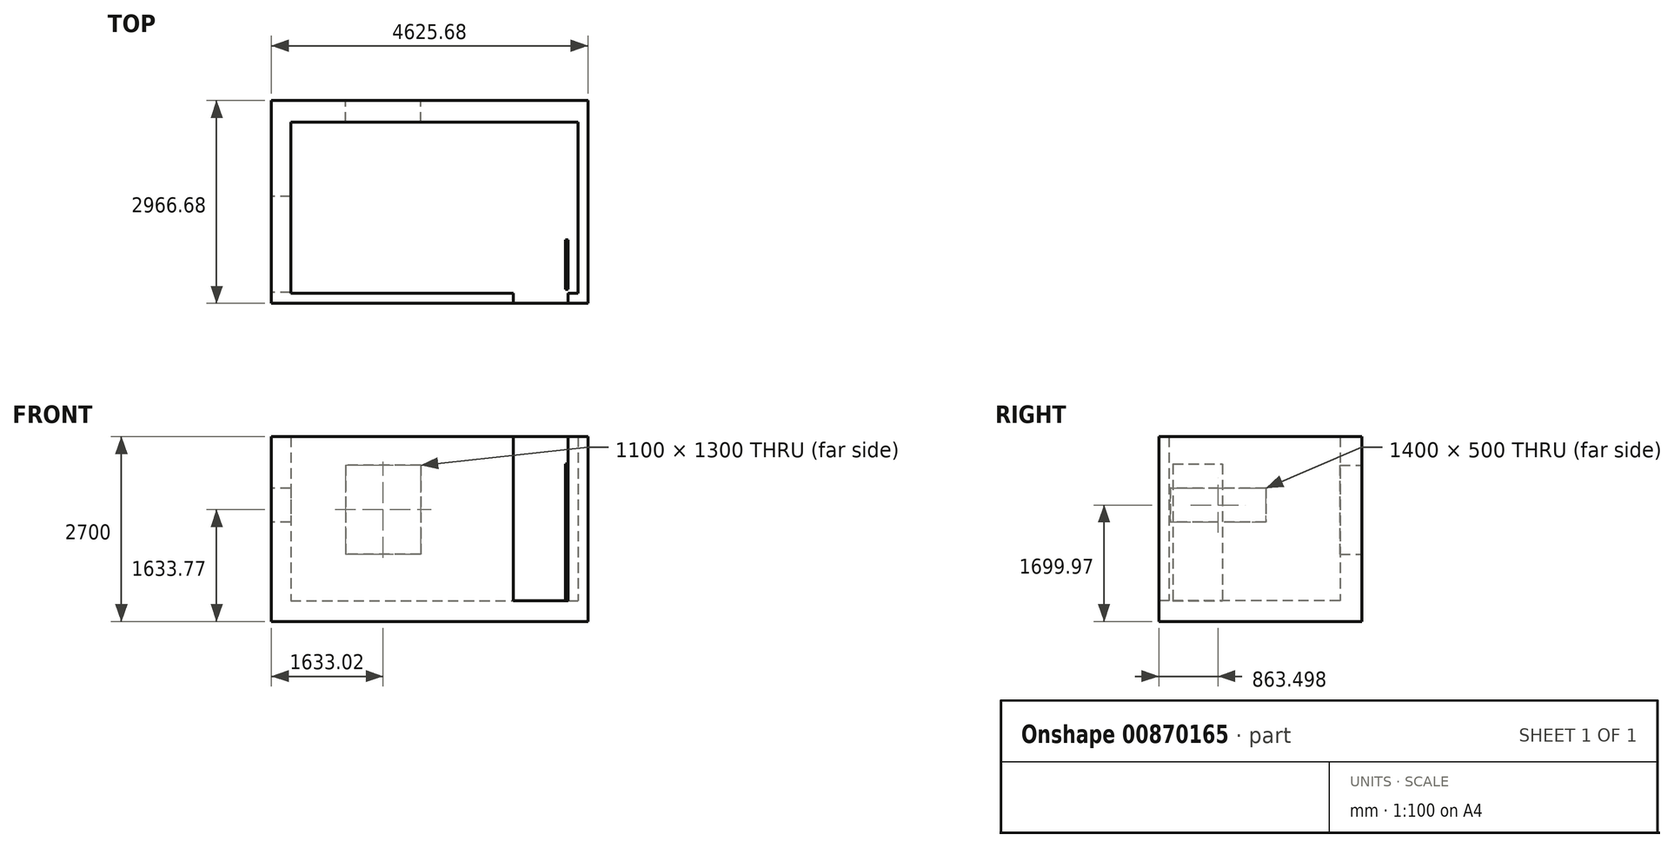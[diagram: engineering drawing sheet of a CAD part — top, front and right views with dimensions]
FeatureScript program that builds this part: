
annotation { "Feature Type Name" : "Feature", "Feature Type Description" : "" }
export const myFeature = defineFeature(function(context is Context, id is Id, definition is map)
    precondition{}
    {
        {
            var Q0;
            Q0=qCreatedBy(makeId("Top.planeOp"),FACE);
            var sketch = newSketch(context, id + "F0", { "sketchPlane" : qUnion([Q0])});
            skLineSegment(sketch, "E0.bottom", {"start": v(6582.95, 22107.28) * mm, "end": v(11208.63, 22107.28) * mm});
            skLineSegment(sketch, "E0.top", {"start": v(6582.95, 19140.6) * mm, "end": v(11208.63, 19140.6) * mm});
            skLineSegment(sketch, "E0.left", {"start": v(6582.95, 22107.28) * mm, "end": v(6582.95, 19140.6) * mm});
            skLineSegment(sketch, "E0.right", {"start": v(11208.63, 22107.28) * mm, "end": v(11208.63, 19140.6) * mm});
            skSolve(sketch);
        }
        {
            var Q0;
            Q0=makeQuery(id+"F0.imprint","IMPRINT",FACE,{"disambiguationData":[TD([[makeQuery(id+"F0.imprint","IMPRINT",EDGE,{"derivedFrom":sQuery(id+"F0.wireOp",EDGE,"E0.bottom")}),-1.0]])]});
            extrude(context, id + "F1", {"entities" : qUnion([Q0]), "oppositeDirection" : true, "depth" : 300 * mm, "offsetDistance" : 25 * mm});
        }
        {
            var Q0;
            Q0=makeQuery(id+"F1.opExtrude","CAP_FACE",FACE,{"disambiguationData":[OSD([sQuery(id+"F0.wireOp",EDGE,"E0.bottom"),sQuery(id+"F0.wireOp",EDGE,"E0.top"),sQuery(id+"F0.wireOp",EDGE,"E0.left"),sQuery(id+"F0.wireOp",EDGE,"E0.right")])],"isStart":true});
            var sketch = newSketch(context, id + "F2", { "sketchPlane" : qUnion([Q0])});
            skLineSegment(sketch, "E1.bottom", {"start": v(6865.03, 21788.88) * mm, "end": v(11065.03, 21788.88) * mm});
            skLineSegment(sketch, "E1.top", {"start": v(6865.03, 19288.88) * mm, "end": v(11065.03, 19288.88) * mm});
            skLineSegment(sketch, "E1.left", {"start": v(6865.03, 21788.88) * mm, "end": v(6865.03, 19288.88) * mm});
            skLineSegment(sketch, "E1.right", {"start": v(11065.03, 21788.88) * mm, "end": v(11065.03, 19288.88) * mm});
            skLineSegment(sketch, "E2", {"start": v(10118.39, 19288.88) * mm, "end": v(10118.39, 19140.6) * mm});
            skLineSegment(sketch, "E3", {"start": v(10918.39, 19288.88) * mm, "end": v(10918.39, 19140.6) * mm});
            skSolve(sketch);
        }
        {
            var Q0;
            Q0=makeQuery(id+"F2.imprint","IMPRINT",FACE,{"disambiguationData":[TD([[makeQuery(id+"F2.imprint","IMPRINT",EDGE,{"derivedFrom":sQuery(id+"F2.wireOp",EDGE,"E1.bottom")}),1.0]])]});
            extrude(context, id + "F3", {"entities" : qUnion([Q0]), "operationType" : NewBodyOperationType.ADD, "depth" : 2400 * mm, "offsetDistance" : 25 * mm});
        }
        {
            var Q0;
            {var subQ0=sQuery(id+"F0.wireOp",EDGE,"E0.bottom");Q0=makeQuery(id+"F3.boolean.opBoolean","MERGE",FACE,{"derivedFrom":[makeQuery(id+"F1.opExtrude","SWEPT_FACE",FACE,{"disambiguationData":[OSD([subQ0])]}),makeQuery(id+"F3.opExtrude","SWEPT_FACE",FACE,{"disambiguationData":[OSD([subQ0])]})]});}
            var sketch = newSketch(context, id + "F4", { "sketchPlane" : qUnion([Q0])});
            skLineSegment(sketch, "E4.bottom", {"start": v(-8765.96, 1983.77) * mm, "end": v(-7665.96, 1983.77) * mm});
            skLineSegment(sketch, "E4.top", {"start": v(-8765.96, 683.77) * mm, "end": v(-7665.96, 683.77) * mm});
            skLineSegment(sketch, "E4.left", {"start": v(-8765.96, 1983.77) * mm, "end": v(-8765.96, 683.77) * mm});
            skLineSegment(sketch, "E4.right", {"start": v(-7665.96, 1983.77) * mm, "end": v(-7665.96, 683.77) * mm});
            skSolve(sketch);
        }
        {
            var Q0;
            Q0=makeQuery(id+"F4.imprint","IMPRINT",FACE,{"disambiguationData":[TD([[makeQuery(id+"F4.imprint","IMPRINT",EDGE,{"derivedFrom":sQuery(id+"F4.wireOp",EDGE,"E4.bottom")}),-1.0]])]});
            extrude(context, id + "F5", {"entities" : qUnion([Q0]), "operationType" : NewBodyOperationType.REMOVE, "endBound" : BoundingType.UP_TO_NEXT, "oppositeDirection" : true, "depth" : 25 * mm, "offsetDistance" : 25 * mm});
        }
        {
            var Q0;
            {var subQ0=sQuery(id+"F0.wireOp",EDGE,"E0.left");Q0=makeQuery(id+"F3.boolean.opBoolean","MERGE",FACE,{"derivedFrom":[makeQuery(id+"F1.opExtrude","SWEPT_FACE",FACE,{"disambiguationData":[OSD([subQ0])]}),makeQuery(id+"F3.opExtrude","SWEPT_FACE",FACE,{"disambiguationData":[OSD([subQ0])]})]});}
            var sketch = newSketch(context, id + "F6", { "sketchPlane" : qUnion([Q0])});
            skLineSegment(sketch, "E5.bottom", {"start": v(-20704.1, 1649.97) * mm, "end": v(-19304.1, 1649.97) * mm});
            skLineSegment(sketch, "E5.top", {"start": v(-20704.1, 1149.97) * mm, "end": v(-19304.1, 1149.97) * mm});
            skLineSegment(sketch, "E5.left", {"start": v(-20704.1, 1649.97) * mm, "end": v(-20704.1, 1149.97) * mm});
            skLineSegment(sketch, "E5.right", {"start": v(-19304.1, 1649.97) * mm, "end": v(-19304.1, 1149.97) * mm});
            skSolve(sketch);
        }
        {
            var Q0;
            Q0=makeQuery(id+"F6.imprint","IMPRINT",FACE,{"disambiguationData":[TD([[makeQuery(id+"F6.imprint","IMPRINT",EDGE,{"derivedFrom":sQuery(id+"F6.wireOp",EDGE,"E5.bottom")}),-1.0]])]});
            extrude(context, id + "F7", {"entities" : qUnion([Q0]), "operationType" : NewBodyOperationType.REMOVE, "endBound" : BoundingType.UP_TO_NEXT, "oppositeDirection" : true, "depth" : 25 * mm, "offsetDistance" : 25 * mm});
        }
        {
            var Q0;
            Q0=makeQuery(id+"F1.opExtrude","CAP_FACE",FACE,{"disambiguationData":[OSD([sQuery(id+"F0.wireOp",EDGE,"E0.bottom"),sQuery(id+"F0.wireOp",EDGE,"E0.top"),sQuery(id+"F0.wireOp",EDGE,"E0.left"),sQuery(id+"F0.wireOp",EDGE,"E0.right")])],"isStart":true});
            var sketch = newSketch(context, id + "F8", { "sketchPlane" : qUnion([Q0])});
            skLineSegment(sketch, "E6.top", {"start": v(10918.39, 20071.87) * mm, "end": v(10879.47, 20071.87) * mm});
            skLineSegment(sketch, "E6.left", {"start": v(10918.39, 19345.94) * mm, "end": v(10918.39, 20071.87) * mm});
            skLineSegment(sketch, "E6.right", {"start": v(10879.47, 19345.94) * mm, "end": v(10879.47, 20071.87) * mm});
            skLineSegment(sketch, "E7", {"start": v(10918.39, 19345.94) * mm, "end": v(10879.47, 19345.94) * mm});
            skSolve(sketch);
        }
        {
            var Q0;
            Q0=makeQuery(id+"F8.imprint","IMPRINT",FACE,{"disambiguationData":[TD([[makeQuery(id+"F8.imprint","IMPRINT",EDGE,{"derivedFrom":sQuery(id+"F8.wireOp",EDGE,"E6.top")}),1.0]])]});
            extrude(context, id + "F9", {"entities" : qUnion([Q0]), "operationType" : NewBodyOperationType.ADD, "depth" : 2000 * mm, "offsetDistance" : 25 * mm});
        }
    });
